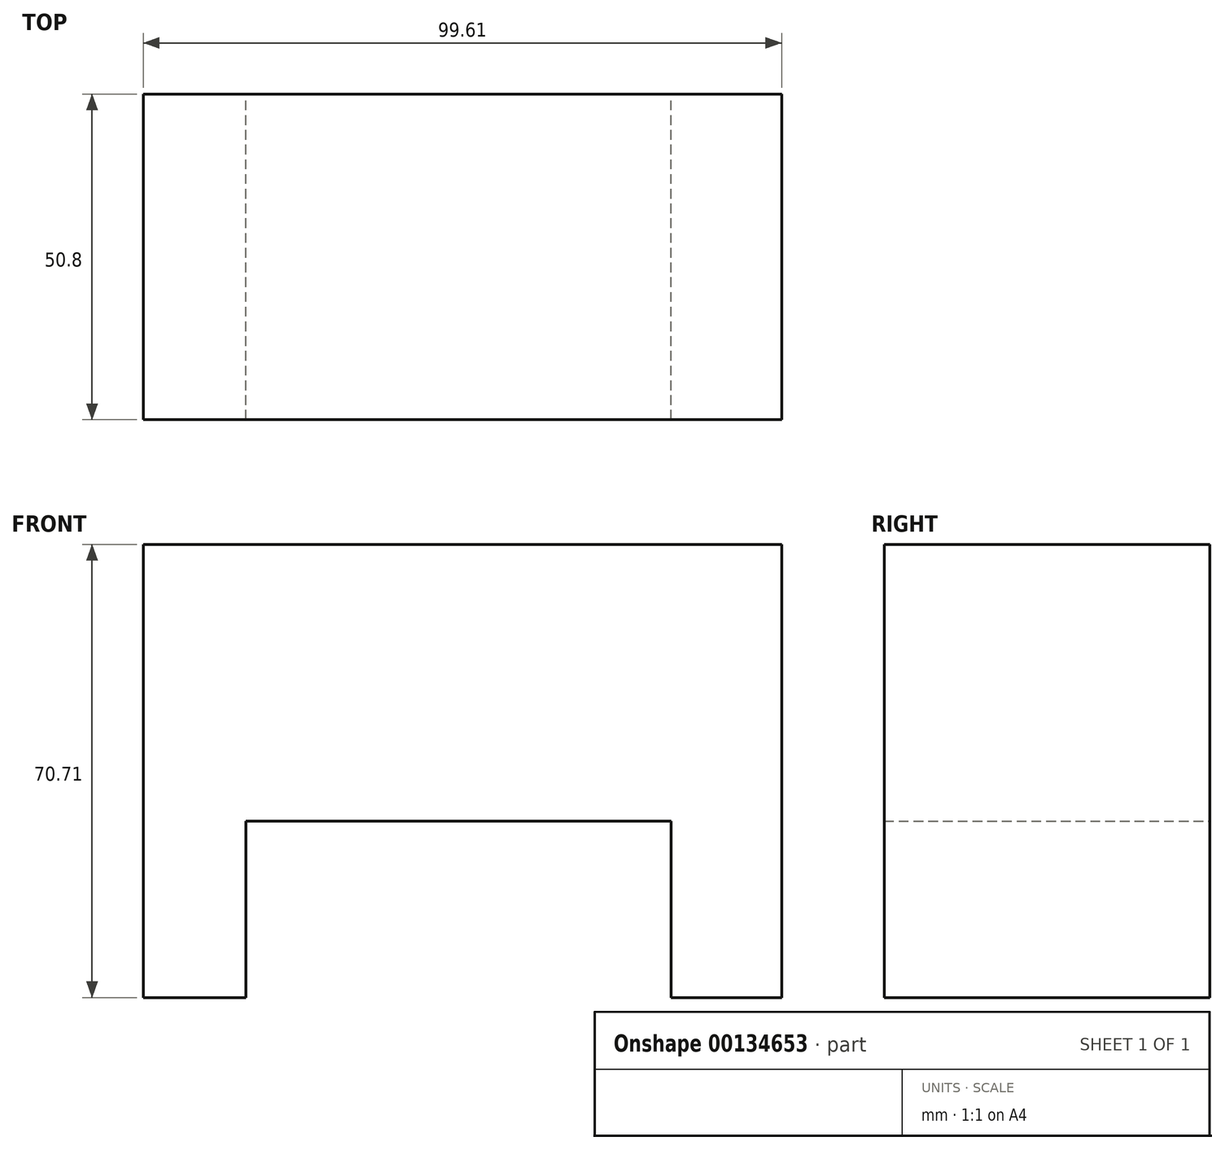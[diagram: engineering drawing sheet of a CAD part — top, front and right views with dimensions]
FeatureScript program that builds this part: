
annotation { "Feature Type Name" : "Feature", "Feature Type Description" : "" }
export const myFeature = defineFeature(function(context is Context, id is Id, definition is map)
    precondition{}
    {
        {
            var Q0;
            Q0=qCreatedBy(makeId("Front.planeOp"),FACE);
            var sketch = newSketch(context, id + "F0", { "sketchPlane" : qUnion([Q0])});
            skLineSegment(sketch, "E0.bottom", {"start": v(-42.46, 23.27) * mm, "end": v(57.15, 23.27) * mm});
            skLineSegment(sketch, "E0.top", {"start": v(-42.46, -47.44) * mm, "end": v(57.15, -47.44) * mm});
            skLineSegment(sketch, "E0.left", {"start": v(-42.46, 23.27) * mm, "end": v(-42.46, -47.44) * mm});
            skLineSegment(sketch, "E0.right", {"start": v(57.15, 23.27) * mm, "end": v(57.15, -47.44) * mm});
            skLineSegment(sketch, "E1", {"start": v(-26.46, -47.44) * mm, "end": v(-26.46, -19.89) * mm});
            skLineSegment(sketch, "E2", {"start": v(-26.46, -19.89) * mm, "end": v(39.93, -19.89) * mm});
            skLineSegment(sketch, "E3", {"start": v(39.93, -19.89) * mm, "end": v(39.93, -47.44) * mm});
            skSolve(sketch);
        }
        {
            var Q0;
            Q0=makeQuery(id+"F0.imprint","IMPRINT",FACE,{"disambiguationData":[TD([[makeQuery(id+"F0.imprint","IMPRINT",EDGE,{"derivedFrom":sQuery(id+"F0.wireOp",EDGE,"E0.bottom")}),-1.0]])]});
            extrude(context, id + "F1", {"entities" : qUnion([Q0]), "depth" : 50.8 * mm});
        }
        {
            var Q0;
            Q0=makeQuery(id+"F1.opExtrude","SWEPT_FACE",FACE,{"disambiguationData":[OSD([sQuery(id+"F0.wireOp",EDGE,"E0.bottom")])]});
            var sketch = newSketch(context, id + "F2", { "sketchPlane" : qUnion([Q0])});
            skCircle(sketch, "E4", {"center": v(3.66, -26.34) * mm, "radius": 13.62 * mm});
            skSolve(sketch);
        }
        {
            var Q0;
            Q0=sQuery(id+"F2.wireOp",EDGE,"E4");
            extrude(context, id + "F3", {"bodyType" : ToolBodyType.SURFACE, "surfaceEntities" : qUnion([Q0]), "depth" : 25.4 * mm});
        }
    });
